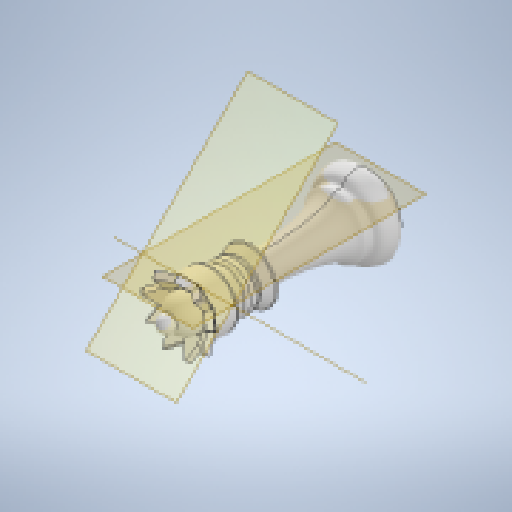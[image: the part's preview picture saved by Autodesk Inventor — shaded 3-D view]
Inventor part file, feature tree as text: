
AUTODESK INVENTOR PART (.ipt)
format: ipt  version: 2024.1 (Build 281209000, 209)  size: 1,186,304 bytes
history: native  units: mm
features: fillet x7, extrude x6, chamfer x6, sketch x6, plane x3, projected_geometry x2, other x1, revolve x1, pattern_circular x1
ambient origin geometry x8: Origin, YZ Plane, XZ Plane, XY Plane, X Axis, Y Axis, Z Axis, Center Point
bodies: Solid1 (feature_tree)
feature tree (33):
  extrude  "Extrusion1"  Depth=10.0mm TaperAngle=0.0deg
  other  "Work Axis1"
  extrude  "Extrusion2"  Depth=46.5mm
  revolve  "Revolution1"  [1 undecoded]
  chamfer  "Chamfer2"  Distance=3.0mm
  fillet  "Fillet1"  Radius=10.0mm
  fillet  "Fillet2"  Radius=4.15mm
  chamfer  "Chamfer3"  Distance=0.4mm
  chamfer  "Chamfer4"  Distance=2.489147mm
  fillet  "Fillet3"  Radius=7.875064mm
  fillet  "Fillet4"  Radius=5.915933mm
  fillet  "Fillet5"  Radius=0.487336mm
  plane  "Work Plane6"
  plane  "Work Plane7"
  plane  "Work Plane8"
  extrude  "Extrusion10"  Depth=0.3mm
  pattern_circular  "Circular Pattern5"  [2 undecoded]
  chamfer  "Chamfer5"  Distance=2.004443mm
  chamfer  "Chamfer6"  Distance=0.435462mm
  fillet  "Fillet7"  Radius=10.0mm
  fillet  "Fillet8"  Radius=8.1mm
  chamfer  "Chamfer1"  Distance=12.6mm
  sketch  "Sketch11"  dims[d9=0.5mm d10=2.0mm d11=45.0deg d40=10.0mm d41=0.0mm d42=4.15mm d43=0.0mm d44=0.4mm d45=0.0mm]
  extrude  "Extrusion6"  Depth=6.3mm
  extrude  "Extrusion7"  Depth=0.3mm
  extrude  "Extrusion8"  Depth=0.3mm
  sketch  "Sketch1"  dims[d0=10.0mm d1=3.0mm d2=0.0mm]
  sketch  "Sketch2"  dims[d3=3.65mm d4=46.5mm]
  sketch  "Sketch3"  dims[d5=360.0deg d6=14.3mm d7=3.0mm d8=0.0mm]
  projected_geometry  "Projected Loop1"
  sketch  "Sketch12"  dims[d51=6.042539mm]
  sketch  "Sketch15"  dims[d52=2.314913mm d53=2.489147mm d54=7.875064mm d55=5.915933mm d57=0.487336mm d58=0.259822mm d59=1.352868mm d60=2.004443mm d61=0.435462mm d64=10.0mm d65=0.0mm d74=8.1mm d75=12.6mm d76=6.3mm d78=5.2mm d79=0.4mm d80=4.4mm d81=9.4mm d82=4.7mm d83=8.9mm d84=10.56mm d85=5.28mm d86=3.17mm d87=10.36mm d88=5.18mm d89=12.3mm d90=6.15mm d91=2.2mm d92=1.5mm d93=2.03mm d94=1.6mm d95=3.17mm d96=6.108652mm d97=1.0mm d98=1.0mm d99=0.1mm d100=3.17mm d101=6.108652mm d102=1.45mm d103=2.0mm d104=6.108652mm d105=1.0mm d106=1.0mm d107=0.6mm d112=1.5mm d113=0.0mm d114=90.0mm d115=360.0deg d118=2.4mm d119=0.1mm d120=2.0mm d121=45.0deg d122=0.2mm d123=2.0mm d124=45.0deg d125=0.5mm d126=0.3mm]
  projected_geometry  "Projected Loop2"
note: 3 required parameter values undecoded (feature->parameter linkage not recoverable at this tier; creation-order binding heuristic only, values carry confidence <= 0.55)